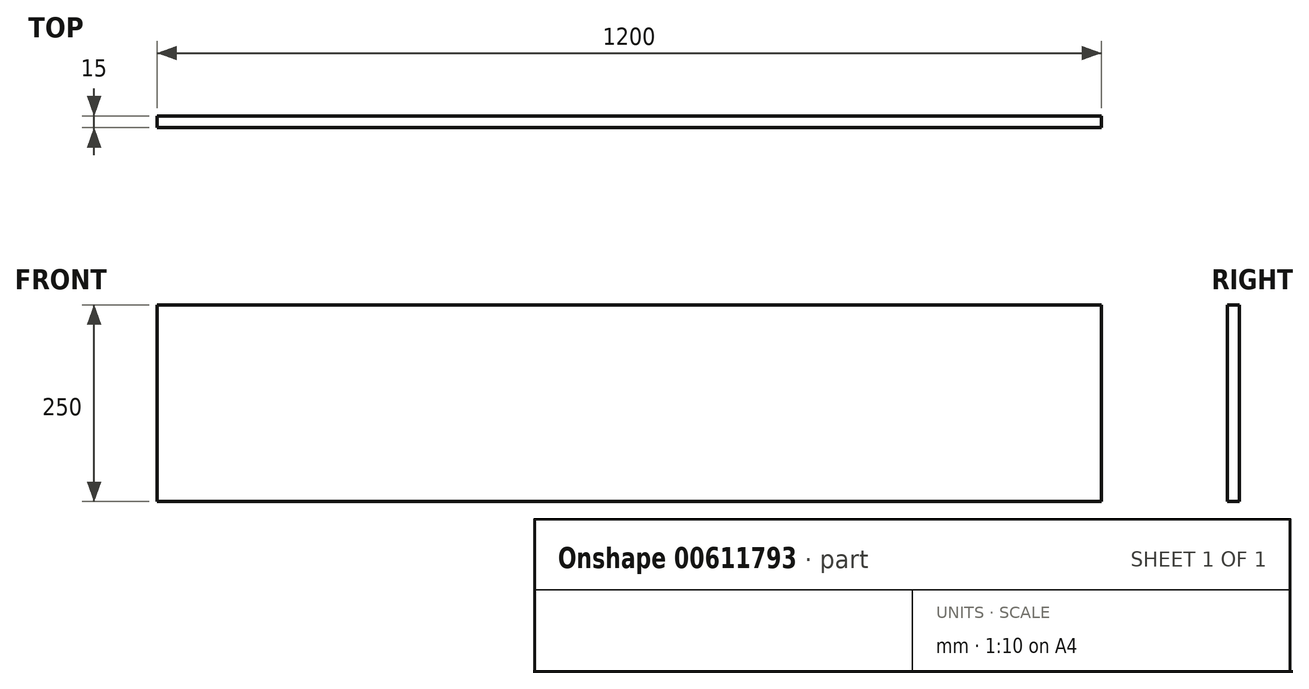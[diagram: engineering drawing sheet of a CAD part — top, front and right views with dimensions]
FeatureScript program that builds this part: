
annotation { "Feature Type Name" : "Feature", "Feature Type Description" : "" }
export const myFeature = defineFeature(function(context is Context, id is Id, definition is map)
    precondition{}
    {
        {
            var Q0;
            Q0=qCreatedBy(makeId("Front.planeOp"),FACE);
            var sketch = newSketch(context, id + "F0", { "sketchPlane" : qUnion([Q0])});
            skLineSegment(sketch, "E0.bottom", {"start": v(-600, 125) * mm, "end": v(600, 125) * mm});
            skLineSegment(sketch, "E0.top", {"start": v(-600, -125) * mm, "end": v(600, -125) * mm});
            skLineSegment(sketch, "E0.left", {"start": v(-600, 125) * mm, "end": v(-600, -125) * mm});
            skLineSegment(sketch, "E0.right", {"start": v(600, 125) * mm, "end": v(600, -125) * mm});
            skPoint(sketch, "E0.middle", {"position": v(0, 0) * mm});
            skSolve(sketch);
        }
        {
            var Q0;
            Q0 = qSketchRegion(id + "F0", true);
            extrude(context, id + "F1", {"entities" : qUnion([Q0]), "depth" : 15 * mm, "offsetDistance" : 25 * mm});
        }
    });
